# Revit family: Compartment_Scranton_Enclosed-Shower-Rabbeted
name_source: partatom
category: Generic Models
units: mm (PartAtom-declared; Revit-internal decimal feet)

## family parameters
Can host rebar = No
Cut with Voids When Loaded = No
Host = Face
Maintain Annotation Orientation = No
Part Type = Normal
Room Calculation Point = No
Round Connector Dimension = Use Diameter
Shared = No

## types (1)
- Compartment_Scranton_Enclosed-Shower-Rabbeted
    Assembly Code = D2010400
    Base Depth = 3' - 0"
    Base Height = 0' - 4"
    Base Width = 3' - 0"
    Corner Left SideBySide Compartment = No
    Corner Right SideBySide Compartment = No
    Default Elevation = 4' - 0"
    Description = Plastic Vanity as Specified
    Expected Lifespan (Years) = 0
    Green Building-LEED = http://www.arcat.com
    Keynote = 10155
    Maintenance Schedule (Months) = 0
    Manufacturer = Scranton Products
    Manufacturer Fax = 800-551-6993
    Manufacturer Website = http://www.scrantonproducts.com
    Middle SideBySide Compartment = No
    Model = As Specified
    Panel Height = 6' - 0"
    Product Data = http://www.arcat.com
    Product Properties = http://www.arcat.com
    Revision = R1_8_2013
    Sales Information = http://www.scrantonproducts.com
    Send Message = http://www.arcat.com
    SpecWizard = http://www.arcat.com
    Specification = http://www.arcat.com
    Standalone Compartment = Yes
    URL = http://www.scrantonproducts.com
    Unit Height = 6' - 4"
    Warranty Duration (Years) = 0
    leftpilasteradjust = 0' - 0"
    leftpilasterwidth = 0' - 4"
    rightpilasteradjust = 0' - 0"
    rightpilasterwidth = 0' - 4"

## geometry (parser evidence)
native form markers: Blend x44, Sweep x2
no freeform markers — native parametric forms only
